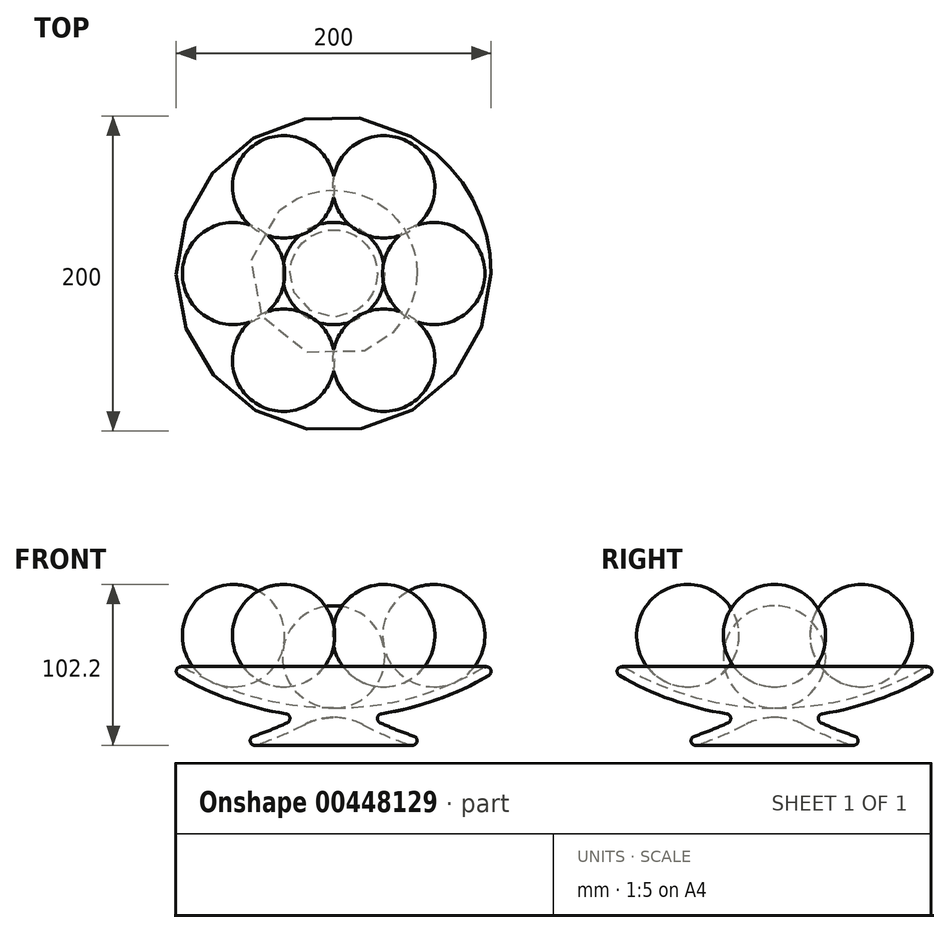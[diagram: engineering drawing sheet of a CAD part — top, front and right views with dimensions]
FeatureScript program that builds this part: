
annotation { "Feature Type Name" : "Feature", "Feature Type Description" : "" }
export const myFeature = defineFeature(function(context is Context, id is Id, definition is map)
    precondition{}
    {
        {
            var Q0;
            Q0=qCreatedBy(makeId("Front.planeOp"),FACE);
            var sketch = newSketch(context, id + "F0", { "sketchPlane" : qUnion([Q0])});
            skCircle(sketch, "E0", {"center": v(0, 38.5) * mm, "radius": 32.5 * mm});
            skCircle(sketch, "E1", {"center": v(-63.58, 52) * mm, "radius": 32.5 * mm});
            skCircle(sketch, "E2", {"center": v(63.58, 52) * mm, "radius": 32.5 * mm});
            skArc(sketch, "E3", {"start": v(-95.48, 31.9) * mm, "mid": v(0, 6) * mm, "end": v(95.48, 31.9) * mm});
            skLineSegment(sketch, "E4", {"start": v(0, 126.54) * mm, "end": v(0, -66.17) * mm, "construction": true});
            skArc(sketch, "E5", {"start": v(-98.52, 26.72) * mm, "mid": v(-65.55, 11.35) * mm, "end": v(-30.3, 2.37) * mm});
            skArc(sketch, "E6", {"start": v(-95.48, 31.9) * mm, "mid": v(-99.59, 30.82) * mm, "end": v(-98.52, 26.72) * mm});
            skArc(sketch, "E7", {"start": v(98.52, 26.72) * mm, "mid": v(99.59, 30.82) * mm, "end": v(95.48, 31.9) * mm});
            skArc(sketch, "E8", {"start": v(29.5, -3.31) * mm, "mid": v(40.1, -7.9) * mm, "end": v(50.94, -11.85) * mm});
            skArc(sketch, "E9", {"start": v(-50.94, -11.85) * mm, "mid": v(-40.1, -7.9) * mm, "end": v(-29.5, -3.31) * mm});
            skArc(sketch, "E10", {"start": v(-50.94, -11.85) * mm, "mid": v(-52.85, -15.64) * mm, "end": v(-49.06, -17.54) * mm});
            skArc(sketch, "E11", {"start": v(49.06, -17.54) * mm, "mid": v(52.85, -15.64) * mm, "end": v(50.94, -11.85) * mm});
            skArc(sketch, "E12", {"start": v(-49.06, -17.54) * mm, "mid": v(-33.58, -11.7) * mm, "end": v(-18.64, -4.6) * mm});
            skArc(sketch, "E13", {"start": v(18.64, -4.6) * mm, "mid": v(33.58, -11.7) * mm, "end": v(49.06, -17.54) * mm});
            skArc(sketch, "E14", {"start": v(18.64, -4.6) * mm, "mid": v(0, 0) * mm, "end": v(-18.64, -4.6) * mm});
            skLineSegment(sketch, "E15", {"start": v(-50, -17.7) * mm, "end": v(50, -17.7) * mm, "construction": true});
            skLineSegment(sketch, "E16", {"start": v(-97, 32.3) * mm, "end": v(97, 32.3) * mm, "construction": true});
            skLineSegment(sketch, "E17", {"start": v(0, 6) * mm, "end": v(0, 0) * mm});
            skArc(sketch, "E18.trimOffspring", {"start": v(30.3, 2.37) * mm, "mid": v(65.55, 11.35) * mm, "end": v(98.52, 26.72) * mm});
            skArc(sketch, "E19", {"start": v(-29.5, -3.31) * mm, "mid": v(-27.8, -0.17) * mm, "end": v(-30.3, 2.37) * mm});
            skArc(sketch, "E20", {"start": v(30.3, 2.37) * mm, "mid": v(27.8, -0.17) * mm, "end": v(29.5, -3.31) * mm});
            skPoint(sketch, "E21.center.orphan", {"position": v(0, -50) * mm});
            skLineSegment(sketch, "E22", {"start": v(-50, -14.7) * mm, "end": v(-50, 32.3) * mm, "construction": true});
            skLineSegment(sketch, "E23", {"start": v(50, -14.7) * mm, "end": v(50, 32.3) * mm, "construction": true});
            skLineSegment(sketch, "E24", {"start": v(0, 71) * mm, "end": v(0, 6) * mm});
            skLineSegment(sketch, "E25", {"start": v(0, 38.5) * mm, "end": v(-63.58, 52) * mm});
            skSolve(sketch);
        }
        {
            var Q0;
            Q0=makeQuery(id+"F0.imprint","IMPRINT",FACE,{"disambiguationData":[TD([[makeQuery(id+"F0.imprint","IMPRINT",EDGE,{"derivedFrom":sQuery(id+"F0.wireOp",EDGE,"E5")}),1.0]])]});
            var Q1;
            {var subQ0=sQuery(id+"F0.wireOp",EDGE,"E24");Q1=makeQuery(id+"F0.imprint","IMPRINT",FACE,{"disambiguationData":[TD([[makeQuery(id+"F0.imprint","IMPRINT",EDGE,{"derivedFrom":subQ0}),-1.0]])]});}
            var Q2;
            Q2=sQuery(id+"F0.wireOp",EDGE,"E4");
            revolve(context, id + "F1", {"entities" : qUnion([Q0, Q1]), "axis" : qUnion([Q2]), "revolveType" : RevolveType.FULL});
        }
        {
            var Q0;
            Q0=makeQuery(id+"F1.opRevolve","SWEPT_BODY",BODY,{"disambiguationData":[OSD([sQuery(id+"F0.wireOp",EDGE,"E0"),sQuery(id+"F0.wireOp",EDGE,"E24")])]});
            var Q1;
            Q1=sQuery(id+"F0.wireOp",EDGE,"E25");
            transform(context, id + "F2", {"entities" : qUnion([Q0]), "transformType" : TransformType.TRANSLATION_ENTITY, "oppositeDirectionEntity" : false, "transformLine" : qUnion([Q1]), "makeCopy" : true});
        }
        {
            var Q0;
            Q0=makeQuery(id+"F2.opPattern","COPY",BODY,{"derivedFrom":makeQuery(id+"F1.opRevolve","SWEPT_BODY",BODY,{"disambiguationData":[OSD([sQuery(id+"F0.wireOp",EDGE,"E0"),sQuery(id+"F0.wireOp",EDGE,"E24")])]}),"instanceName":"1"});
            var Q1;
            Q1=sQuery(id+"F0.wireOp",EDGE,"E4");
            circularPattern(context, id + "F3", {"entities" : qUnion([Q0]), "axis" : qUnion([Q1]), "angle" : 360 * degree, "instanceCount" : 6, "equalSpace" : true});
        }
    });
